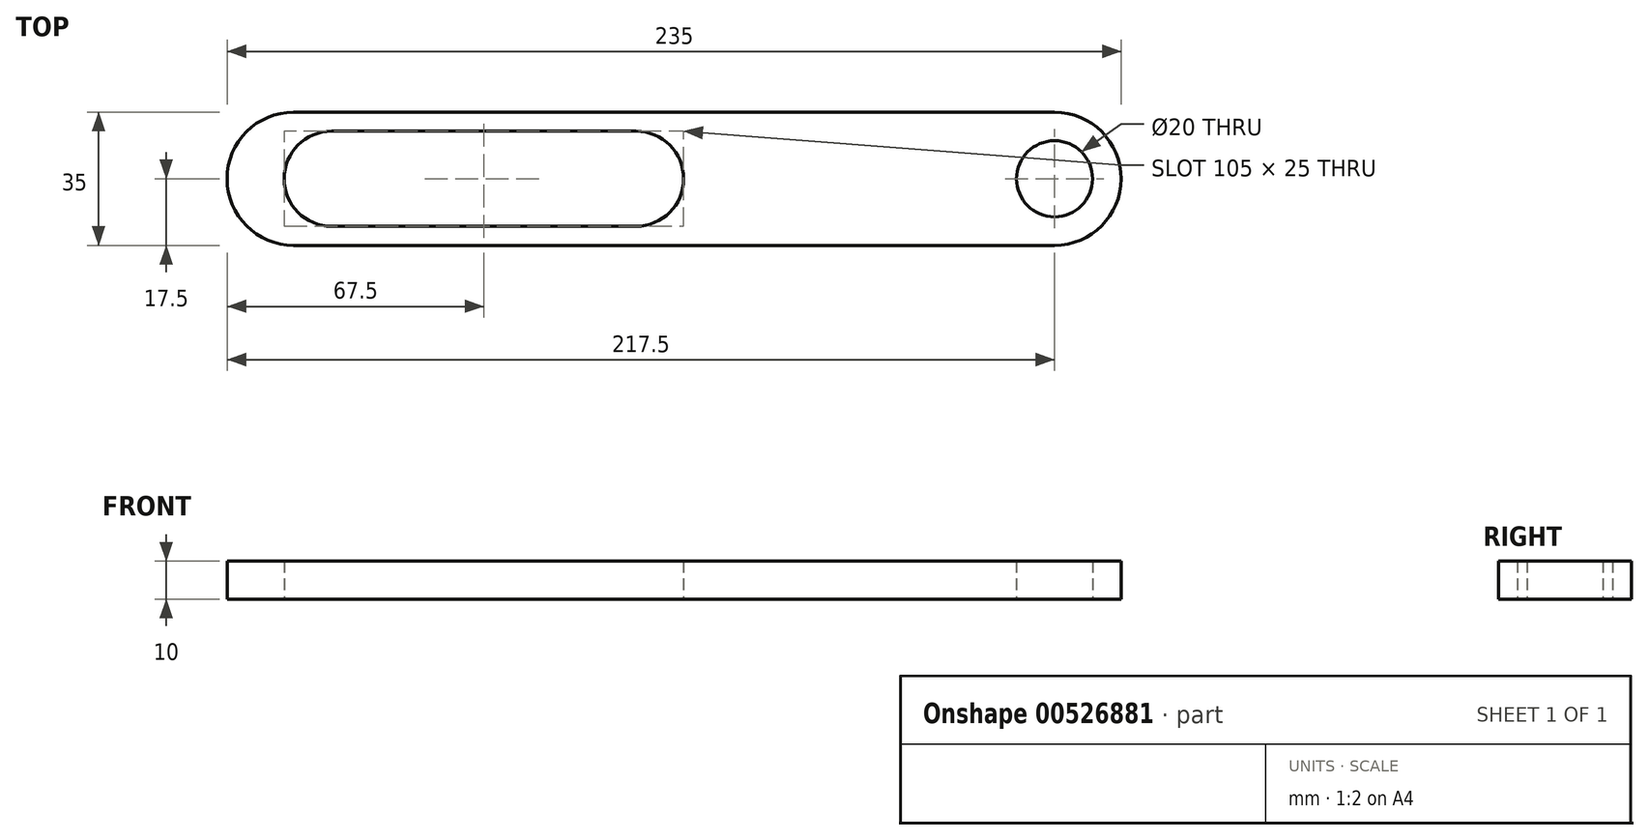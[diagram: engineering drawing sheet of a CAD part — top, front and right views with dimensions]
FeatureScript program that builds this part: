
annotation { "Feature Type Name" : "Feature", "Feature Type Description" : "" }
export const myFeature = defineFeature(function(context is Context, id is Id, definition is map)
    precondition{}
    {
        {
            var Q0;
            Q0=qCreatedBy(makeId("Top.planeOp"),FACE);
            var sketch = newSketch(context, id + "F0", { "sketchPlane" : qUnion([Q0])});
            skLineSegment(sketch, "E0.bottom", {"start": v(-100, 17.5) * mm, "end": v(100, 17.5) * mm});
            skLineSegment(sketch, "E0.top", {"start": v(-100, -17.5) * mm, "end": v(100, -17.5) * mm});
            skPoint(sketch, "E0.middle", {"position": v(0, 0) * mm});
            skLineSegment(sketch, "E1.bottom", {"start": v(-90, 12.5) * mm, "end": v(-10, 12.5) * mm});
            skLineSegment(sketch, "E1.top", {"start": v(-90, -12.5) * mm, "end": v(-10, -12.5) * mm});
            skPoint(sketch, "E1.middle", {"position": v(-50, 0) * mm});
            skArc(sketch, "E2", {"start": v(-100, 17.5) * mm, "mid": v(-117.5, 0) * mm, "end": v(-100, -17.5) * mm});
            skArc(sketch, "E3", {"start": v(100, -17.5) * mm, "mid": v(117.5, 0) * mm, "end": v(100, 17.5) * mm});
            skArc(sketch, "E4", {"start": v(-90, 12.5) * mm, "mid": v(-102.5, 0) * mm, "end": v(-90, -12.5) * mm});
            skArc(sketch, "E5", {"start": v(-10, -12.5) * mm, "mid": v(2.5, 0) * mm, "end": v(-10, 12.5) * mm});
            skCircle(sketch, "E6", {"center": v(100, 0) * mm, "radius": 10 * mm});
            skSolve(sketch);
        }
        {
            var Q0;
            Q0 = qSketchRegion(id + "F0", true);
            extrude(context, id + "F1", {"entities" : qUnion([Q0]), "endBound" : BoundingType.SYMMETRIC, "depth" : 10 * mm, "offsetDistance" : 25.4 * mm});
        }
    });
